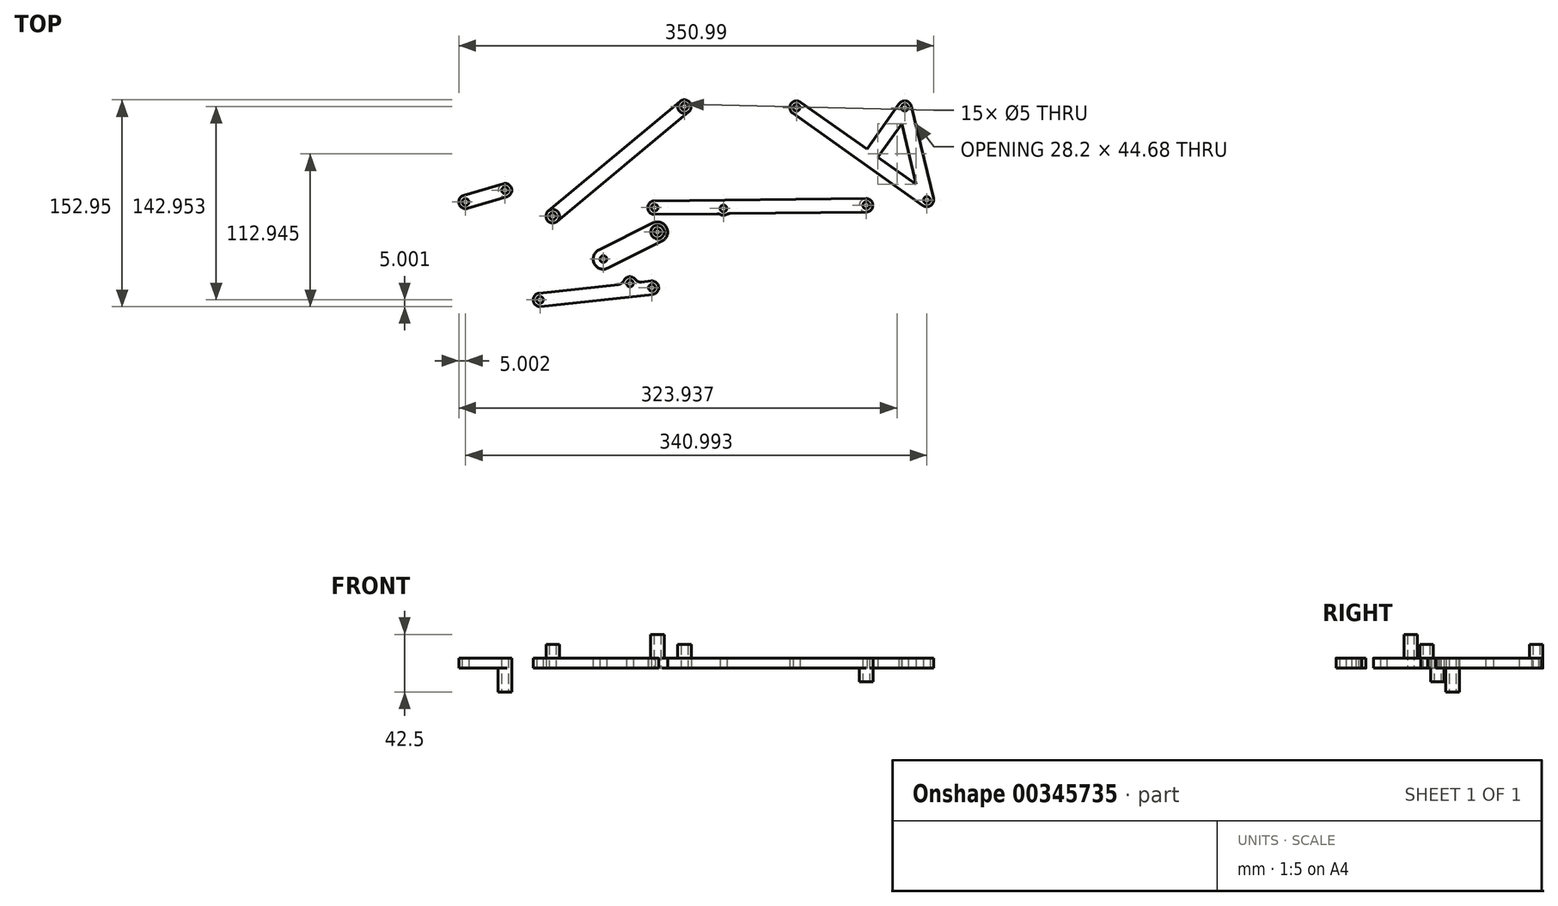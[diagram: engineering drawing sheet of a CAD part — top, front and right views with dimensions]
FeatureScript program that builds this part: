
annotation { "Feature Type Name" : "Feature", "Feature Type Description" : "" }
export const myFeature = defineFeature(function(context is Context, id is Id, definition is map)
    precondition{}
    {
        {
            var Q0;
            Q0=qCreatedBy(makeId("Top.planeOp"),FACE);
            var sketch = newSketch(context, id + "F0", { "sketchPlane" : qUnion([Q0])});
            skLineSegment(sketch, "E0", {"start": v(-4.13, -41.2) * mm, "end": v(-86.83, -50.14) * mm});
            skLineSegment(sketch, "E1", {"start": v(-20.32, -38.04) * mm, "end": v(-86.83, -50.14) * mm});
            skLineSegment(sketch, "E2", {"start": v(-20.32, -38.04) * mm, "end": v(-4.13, -41.2) * mm});
            skCircle(sketch, "E3", {"center": v(-20.32, -38.04) * mm, "radius": 2.5 * mm});
            skCircle(sketch, "E4", {"center": v(-86.83, -50.14) * mm, "radius": 2.5 * mm});
            skCircle(sketch, "E5", {"center": v(-4.13, -41.2) * mm, "radius": 2.5 * mm});
            skLineSegment(sketch, "E6", {"start": v(-20.32, -38.04) * mm, "end": v(-19.44, -42.85) * mm});
            skArc(sketch, "E7.0.startCap", {"start": v(-25.3, -38.46) * mm, "mid": v(-20.98, -33.08) * mm, "end": v(-15.4, -37.14) * mm});
            skArc(sketch, "E7.0.endCap", {"start": v(-14.52, -41.96) * mm, "mid": v(-18.55, -47.77) * mm, "end": v(-24.36, -43.75) * mm});
            skLineSegment(sketch, "E7.0.left", {"start": v(-15.4, -37.14) * mm, "end": v(-14.52, -41.96) * mm});
            skLineSegment(sketch, "E7.0.right", {"start": v(-25.24, -38.93) * mm, "end": v(-24.36, -43.75) * mm});
            skArc(sketch, "E7.1.startCap", {"start": v(-4.66, -36.23) * mm, "mid": v(0.85, -40.66) * mm, "end": v(-3.59, -46.17) * mm});
            skArc(sketch, "E7.1.endCap", {"start": v(-86.3, -55.1) * mm, "mid": v(-91.8, -50.68) * mm, "end": v(-87.37, -45.17) * mm});
            skLineSegment(sketch, "E7.1.left", {"start": v(-3.59, -46.17) * mm, "end": v(-86.3, -55.1) * mm});
            skLineSegment(sketch, "E7.1.right", {"start": v(-4.66, -36.23) * mm, "end": v(-15.35, -37.38) * mm});
            skLineSegment(sketch, "E8.trimOffspring", {"start": v(-25.3, -38.46) * mm, "end": v(-87.37, -45.17) * mm});
            skLineSegment(sketch, "E9.trimOffspring", {"start": v(-17.85, -37.65) * mm, "end": v(-22.81, -38.19) * mm});
            skSolve(sketch);
        }
        {
            var Q0;
            Q0 = qSketchRegion(id + "F0", true);
            var Q1;
            {var subQ0=sQuery(id+"F0.wireOp",EDGE,"E7.0.right");var subQ1=sQuery(id+"F0.wireOp",EDGE,"E0");var subQ2=makeQuery(id+"F0.imprint","INTERSECT",VERTEX,{"derivedFrom":[subQ1,subQ0]});Q1=makeQuery(id+"F0.imprint","IMPRINT",FACE,{"disambiguationData":[TD([[makeQuery(id+"F0.imprint","IMPRINT",EDGE,{"disambiguationData":[TD([[subQ2,-1.0]])],"derivedFrom":subQ1}),-1.0]])]});}
            var Q2;
            {var subQ0=sQuery(id+"F0.wireOp",EDGE,"E6");var subQ1=sQuery(id+"F0.wireOp",EDGE,"E0");var subQ2=makeQuery(id+"F0.imprint","INTERSECT",VERTEX,{"derivedFrom":[subQ1,subQ0]});Q2=makeQuery(id+"F0.imprint","IMPRINT",FACE,{"disambiguationData":[TD([[makeQuery(id+"F0.imprint","IMPRINT",EDGE,{"disambiguationData":[TD([[subQ2,-1.0]])],"derivedFrom":subQ1}),-1.0]])]});}
            var Q3;
            {var subQ0=sQuery(id+"F0.wireOp",EDGE,"E6");var subQ1=sQuery(id+"F0.wireOp",EDGE,"E0");var subQ2=makeQuery(id+"F0.imprint","INTERSECT",VERTEX,{"derivedFrom":[subQ1,subQ0]});Q3=makeQuery(id+"F0.imprint","IMPRINT",FACE,{"disambiguationData":[TD([[makeQuery(id+"F0.imprint","IMPRINT",EDGE,{"disambiguationData":[TD([[subQ2,1.0]])],"derivedFrom":subQ1}),-1.0]])]});}
            var Q4;
            {var subQ3=sQuery(id+"F0.wireOp",EDGE,"E5");var subQ5=sQuery(id+"F0.wireOp",EDGE,"E0");var subQ6=makeQuery(id+"F0.imprint","INTERSECT",VERTEX,{"derivedFrom":[subQ5,subQ3]});Q4=makeQuery(id+"F0.imprint","IMPRINT",FACE,{"disambiguationData":[TD([[makeQuery(id+"F0.imprint","IMPRINT",EDGE,{"disambiguationData":[TD([[subQ6,-1.0]])],"derivedFrom":subQ5}),-1.0]])]});}
            extrude(context, id + "F1", {"entities" : qUnion([Q0, Q1, Q2, Q3, Q4]), "depth" : 7.5 * mm});
        }
        {
            var Q0;
            Q0=makeQuery(id+"F1.opExtrude","SWEPT_EDGE",EDGE,{"disambiguationData":[OSD([sQuery(id+"F0.wireOp",EDGE,"E7.0.left"),sQuery(id+"F0.wireOp",EDGE,"E7.1.right")])]});
            var Q1;
            Q1=makeQuery(id+"F1.opExtrude","SWEPT_EDGE",EDGE,{"disambiguationData":[OSD([sQuery(id+"F0.wireOp",EDGE,"E7.0.startCap"),sQuery(id+"F0.wireOp",EDGE,"E8.trimOffspring")])]});
            fillet(context, id + "F2", {"entities" : qUnion([Q0, Q1]), "radius" : 5 * mm, "tangentPropagation" : true, "allowEdgeOverflow" : false});
        }
        {
            var Q0;
            Q0=qCreatedBy(makeId("Top.planeOp"),FACE);
            var sketch = newSketch(context, id + "F3", { "sketchPlane" : qUnion([Q0])});
            skLineSegment(sketch, "E10", {"start": v(-2.13, 18.04) * mm, "end": v(154.22, 19.78) * mm});
            skLineSegment(sketch, "E11", {"start": v(48.77, 17.41) * mm, "end": v(-2.13, 18.04) * mm});
            skLineSegment(sketch, "E12", {"start": v(48.77, 17.41) * mm, "end": v(154.22, 19.78) * mm});
            skCircle(sketch, "E13", {"center": v(-2.13, 18.04) * mm, "radius": 2.5 * mm});
            skCircle(sketch, "E14", {"center": v(48.77, 17.41) * mm, "radius": 2.5 * mm});
            skCircle(sketch, "E15", {"center": v(154.22, 19.78) * mm, "radius": 2.5 * mm});
            skLineSegment(sketch, "E16", {"start": v(48.77, 17.41) * mm, "end": v(48.75, 18.6) * mm});
            skArc(sketch, "E17.0.startCap", {"start": v(-2.07, 13.04) * mm, "mid": v(-7.13, 17.99) * mm, "end": v(-2.18, 23.04) * mm});
            skArc(sketch, "E17.0.endCap", {"start": v(154.16, 24.78) * mm, "mid": v(159.22, 19.83) * mm, "end": v(154.28, 14.78) * mm});
            skLineSegment(sketch, "E17.0.left", {"start": v(-2.18, 23.04) * mm, "end": v(154.16, 24.78) * mm});
            skLineSegment(sketch, "E17.0.right", {"start": v(-2.07, 13.04) * mm, "end": v(154.28, 14.78) * mm});
            skArc(sketch, "E17.1.startCap", {"start": v(53.77, 17.53) * mm, "mid": v(48.89, 12.42) * mm, "end": v(43.78, 17.3) * mm});
            skArc(sketch, "E17.1.endCap", {"start": v(43.75, 18.5) * mm, "mid": v(48.64, 23.6) * mm, "end": v(53.75, 18.72) * mm});
            skLineSegment(sketch, "E17.1.left", {"start": v(43.78, 17.3) * mm, "end": v(43.75, 18.5) * mm});
            skLineSegment(sketch, "E17.1.right", {"start": v(53.77, 17.53) * mm, "end": v(53.75, 18.72) * mm});
            skSolve(sketch);
        }
        {
            var Q0;
            Q0 = qSketchRegion(id + "F3", true);
            var Q1;
            {var subQ0=sQuery(id+"F3.wireOp",EDGE,"E17.1.right");var subQ1=sQuery(id+"F3.wireOp",EDGE,"E10");var subQ2=makeQuery(id+"F3.imprint","INTERSECT",VERTEX,{"derivedFrom":[subQ1,subQ0]});Q1=makeQuery(id+"F3.imprint","IMPRINT",FACE,{"disambiguationData":[TD([[makeQuery(id+"F3.imprint","IMPRINT",EDGE,{"disambiguationData":[TD([[subQ2,-1.0]])],"derivedFrom":subQ1}),-1.0]])]});}
            var Q2;
            {var subQ1=sQuery(id+"F3.wireOp",EDGE,"E17.1.endCap");var subQ3=sQuery(id+"F3.wireOp",EDGE,"E10");var subQ4=makeQuery(id+"F3.imprint","INTERSECT",VERTEX,{"derivedFrom":[subQ3,subQ1]});Q2=makeQuery(id+"F3.imprint","IMPRINT",FACE,{"disambiguationData":[TD([[makeQuery(id+"F3.imprint","IMPRINT",EDGE,{"disambiguationData":[TD([[subQ4,-1.0]])],"derivedFrom":subQ3}),-1.0]])]});}
            var Q3;
            {var subQ0=sQuery(id+"F3.wireOp",EDGE,"E13");var subQ1=sQuery(id+"F3.wireOp",EDGE,"E10");var subQ2=makeQuery(id+"F3.imprint","INTERSECT",VERTEX,{"derivedFrom":[subQ1,subQ0]});Q3=makeQuery(id+"F3.imprint","IMPRINT",FACE,{"disambiguationData":[TD([[makeQuery(id+"F3.imprint","IMPRINT",EDGE,{"disambiguationData":[TD([[subQ2,-1.0]])],"derivedFrom":subQ1}),-1.0]])]});}
            var Q4;
            {var subQ0=sQuery(id+"F3.wireOp",EDGE,"E14");var subQ1=sQuery(id+"F3.wireOp",EDGE,"E10");var subQ2=makeQuery(id+"F3.imprint","INTERSECT",VERTEX,{"disambiguationData":[OD(1.0)],"derivedFrom":[subQ1,subQ0]});Q4=makeQuery(id+"F3.imprint","IMPRINT",FACE,{"disambiguationData":[TD([[makeQuery(id+"F3.imprint","IMPRINT",EDGE,{"disambiguationData":[TD([[subQ2,-1.0]])],"derivedFrom":subQ1}),-1.0]])]});}
            extrude(context, id + "F4", {"entities" : qUnion([Q0, Q1, Q2, Q3, Q4]), "depth" : 7.5 * mm});
        }
        {
            var Q0;
            {var subQ0=sQuery(id+"F3.wireOp",EDGE,"E17.1.startCap");var subQ1=sQuery(id+"F3.wireOp",EDGE,"E17.0.right");Q0=makeQuery(id+"F4.opExtrude","SWEPT_EDGE",EDGE,{"disambiguationData":[OSD([subQ1,subQ0]),TDD([makeQuery(id+"F3.imprint","INTERSECT",VERTEX,{"disambiguationData":[OD(0.0)],"derivedFrom":[subQ1,subQ0]})])]});}
            var Q1;
            {var subQ0=sQuery(id+"F3.wireOp",EDGE,"E17.1.startCap");var subQ1=sQuery(id+"F3.wireOp",EDGE,"E17.0.right");Q1=makeQuery(id+"F4.opExtrude","SWEPT_EDGE",EDGE,{"disambiguationData":[OSD([subQ1,subQ0]),TDD([makeQuery(id+"F3.imprint","INTERSECT",VERTEX,{"disambiguationData":[OD(1.0)],"derivedFrom":[subQ1,subQ0]})])]});}
            fillet(context, id + "F5", {"entities" : qUnion([Q0, Q1]), "radius" : 5 * mm, "tangentPropagation" : true, "allowEdgeOverflow" : false});
        }
        {
            var Q0;
            Q0=qCreatedBy(makeId("Top.planeOp"),FACE);
            var sketch = newSketch(context, id + "F6", { "sketchPlane" : qUnion([Q0])});
            skLineSegment(sketch, "E18", {"start": v(19.9, 92.81) * mm, "end": v(-77.4, 11.71) * mm});
            skLineSegment(sketch, "E19", {"start": v(-141.85, 22.22) * mm, "end": v(-112.7, 30.91) * mm});
            skCircle(sketch, "E20", {"center": v(-141.85, 22.22) * mm, "radius": 2.5 * mm});
            skCircle(sketch, "E21", {"center": v(-112.7, 30.91) * mm, "radius": 2.5 * mm});
            skCircle(sketch, "E22", {"center": v(-77.4, 11.71) * mm, "radius": 2.5 * mm});
            skCircle(sketch, "E23", {"center": v(19.9, 92.81) * mm, "radius": 2.5 * mm});
            skArc(sketch, "E24.0.startCap", {"start": v(16.7, 96.65) * mm, "mid": v(23.74, 96.02) * mm, "end": v(23.1, 88.97) * mm});
            skArc(sketch, "E24.0.endCap", {"start": v(-74.2, 7.87) * mm, "mid": v(-81.23, 8.51) * mm, "end": v(-80.6, 15.55) * mm});
            skLineSegment(sketch, "E24.0.left", {"start": v(23.1, 88.97) * mm, "end": v(-74.2, 7.87) * mm});
            skLineSegment(sketch, "E24.0.right", {"start": v(16.7, 96.65) * mm, "end": v(-80.6, 15.55) * mm});
            skArc(sketch, "E25.0.startCap", {"start": v(-140.42, 17.43) * mm, "mid": v(-146.64, 20.79) * mm, "end": v(-143.28, 27) * mm});
            skArc(sketch, "E25.0.endCap", {"start": v(-114.12, 35.7) * mm, "mid": v(-107.9, 32.34) * mm, "end": v(-111.26, 26.12) * mm});
            skLineSegment(sketch, "E25.0.left", {"start": v(-143.28, 27) * mm, "end": v(-114.12, 35.7) * mm});
            skLineSegment(sketch, "E25.0.right", {"start": v(-140.42, 17.43) * mm, "end": v(-111.26, 26.12) * mm});
            skSolve(sketch);
        }
        {
            var Q0;
            Q0 = qSketchRegion(id + "F6", true);
            extrude(context, id + "F7", {"entities" : qUnion([Q0]), "depth" : 7.5 * mm});
        }
        {
            var Q0;
            Q0=qCreatedBy(makeId("Top.planeOp"),FACE);
            var sketch = newSketch(context, id + "F8", { "sketchPlane" : qUnion([Q0])});
            skLineSegment(sketch, "E26", {"start": v(199.14, 23.7) * mm, "end": v(102.8, 92) * mm, "construction": true});
            skLineSegment(sketch, "E27", {"start": v(102.8, 92) * mm, "end": v(182.8, 92) * mm, "construction": true});
            skLineSegment(sketch, "E28", {"start": v(182.8, 92) * mm, "end": v(199.14, 23.7) * mm, "construction": true});
            skCircle(sketch, "E29", {"center": v(102.8, 92) * mm, "radius": 2.5 * mm});
            skCircle(sketch, "E30", {"center": v(182.8, 92) * mm, "radius": 2.5 * mm});
            skCircle(sketch, "E31", {"center": v(199.14, 23.7) * mm, "radius": 2.5 * mm});
            skArc(sketch, "E32.0.startCap", {"start": v(102.8, 87) * mm, "mid": v(97.8, 92) * mm, "end": v(102.8, 97) * mm});
            skArc(sketch, "E32.0.endCap", {"start": v(182.8, 97) * mm, "mid": v(187.8, 92) * mm, "end": v(182.8, 87) * mm});
            skLineSegment(sketch, "E32.0.left", {"start": v(102.8, 97) * mm, "end": v(182.8, 97) * mm, "construction": true});
            skLineSegment(sketch, "E32.0.right", {"start": v(102.8, 87) * mm, "end": v(182.8, 87) * mm, "construction": true});
            skArc(sketch, "E32.1.startCap", {"start": v(177.93, 90.84) * mm, "mid": v(181.63, 96.86) * mm, "end": v(187.66, 93.17) * mm});
            skArc(sketch, "E32.1.endCap", {"start": v(204, 24.86) * mm, "mid": v(200.3, 18.83) * mm, "end": v(194.28, 22.53) * mm});
            skLineSegment(sketch, "E32.1.left", {"start": v(187.66, 93.17) * mm, "end": v(204, 24.86) * mm});
            skLineSegment(sketch, "E32.1.right", {"start": v(177.93, 90.84) * mm, "end": v(194.28, 22.53) * mm});
            skArc(sketch, "E32.2.startCap", {"start": v(202.04, 27.77) * mm, "mid": v(203.22, 20.8) * mm, "end": v(196.25, 19.61) * mm});
            skArc(sketch, "E32.2.endCap", {"start": v(99.9, 87.92) * mm, "mid": v(98.72, 94.9) * mm, "end": v(105.69, 96.08) * mm});
            skLineSegment(sketch, "E32.2.left", {"start": v(196.25, 19.61) * mm, "end": v(99.9, 87.92) * mm});
            skLineSegment(sketch, "E32.2.right", {"start": v(202.04, 27.77) * mm, "end": v(105.69, 96.08) * mm});
            skLineSegment(sketch, "E33", {"start": v(178.93, 95.17) * mm, "end": v(154.86, 61.22) * mm});
            skLineSegment(sketch, "E34", {"start": v(186.58, 88.74) * mm, "end": v(162.99, 55.46) * mm});
            skSolve(sketch);
        }
        {
            var Q0;
            Q0 = qSketchRegion(id + "F8", true);
            var Q1;
            {var subQ5=sQuery(id+"F8.wireOp",EDGE,"E27");var subQ7=sQuery(id+"F8.wireOp",EDGE,"E32.2.right");var subQ8=makeQuery(id+"F8.imprint","INTERSECT",VERTEX,{"derivedFrom":[subQ5,subQ7]});Q1=makeQuery(id+"F8.imprint","IMPRINT",FACE,{"disambiguationData":[TD([[makeQuery(id+"F8.imprint","IMPRINT",EDGE,{"disambiguationData":[TD([[subQ8,-1.0]])],"derivedFrom":subQ5}),-1.0]])]});}
            var Q2;
            {var subQ0=sQuery(id+"F8.wireOp",EDGE,"E32.1.right");var subQ1=sQuery(id+"F8.wireOp",EDGE,"E26");var subQ2=makeQuery(id+"F8.imprint","INTERSECT",VERTEX,{"derivedFrom":[subQ1,subQ0]});Q2=makeQuery(id+"F8.imprint","IMPRINT",FACE,{"disambiguationData":[TD([[makeQuery(id+"F8.imprint","IMPRINT",EDGE,{"disambiguationData":[TD([[subQ2,-1.0]])],"derivedFrom":subQ1}),-1.0]])]});}
            var Q3;
            {var subQ5=sQuery(id+"F8.wireOp",EDGE,"E32.0.endCap");var subQ7=sQuery(id+"F8.wireOp",EDGE,"E28");var subQ8=makeQuery(id+"F8.imprint","INTERSECT",VERTEX,{"derivedFrom":[subQ7,subQ5]});Q3=makeQuery(id+"F8.imprint","IMPRINT",FACE,{"disambiguationData":[TD([[makeQuery(id+"F8.imprint","IMPRINT",EDGE,{"disambiguationData":[TD([[subQ8,-1.0]])],"derivedFrom":subQ7}),-1.0]])]});}
            var Q4;
            {var subQ1=sQuery(id+"F8.wireOp",EDGE,"E27");var subQ11=sQuery(id+"F8.wireOp",EDGE,"E32.1.startCap");var subQ13=makeQuery(id+"F8.imprint","INTERSECT",VERTEX,{"derivedFrom":[subQ1,subQ11]});Q4=makeQuery(id+"F8.imprint","IMPRINT",FACE,{"disambiguationData":[TD([[makeQuery(id+"F8.imprint","IMPRINT",EDGE,{"disambiguationData":[TD([[subQ13,-1.0]])],"derivedFrom":subQ1}),-1.0]])]});}
            var Q5;
            {var subQ0=sQuery(id+"F8.wireOp",EDGE,"E31");var subQ1=sQuery(id+"F8.wireOp",EDGE,"E26");var subQ2=makeQuery(id+"F8.imprint","INTERSECT",VERTEX,{"derivedFrom":[subQ1,subQ0]});Q5=makeQuery(id+"F8.imprint","IMPRINT",FACE,{"disambiguationData":[TD([[makeQuery(id+"F8.imprint","IMPRINT",EDGE,{"disambiguationData":[TD([[subQ2,-1.0]])],"derivedFrom":subQ1}),-1.0]])]});}
            var Q6;
            {var subQ0=sQuery(id+"F8.wireOp",EDGE,"E34");var subQ1=sQuery(id+"F8.wireOp",EDGE,"E28");var subQ2=makeQuery(id+"F8.imprint","INTERSECT",VERTEX,{"derivedFrom":[subQ1,subQ0]});Q6=makeQuery(id+"F8.imprint","IMPRINT",FACE,{"disambiguationData":[TD([[makeQuery(id+"F8.imprint","IMPRINT",EDGE,{"disambiguationData":[TD([[subQ2,-1.0]])],"derivedFrom":subQ1}),-1.0]])]});}
            var Q7;
            {var subQ0=sQuery(id+"F8.wireOp",EDGE,"E32.0.endCap");var subQ1=sQuery(id+"F8.wireOp",EDGE,"E28");var subQ2=makeQuery(id+"F8.imprint","INTERSECT",VERTEX,{"derivedFrom":[subQ1,subQ0]});Q7=makeQuery(id+"F8.imprint","IMPRINT",FACE,{"disambiguationData":[TD([[makeQuery(id+"F8.imprint","IMPRINT",EDGE,{"disambiguationData":[TD([[subQ2,-1.0]])],"derivedFrom":subQ1}),1.0]])]});}
            extrude(context, id + "F9", {"entities" : qUnion([Q0, Q1, Q2, Q3, Q4, Q5, Q6, Q7]), "depth" : 7.5 * mm});
        }
        {
            var Q0;
            Q0=qCreatedBy(makeId("Top.planeOp"),FACE);
            var sketch = newSketch(context, id + "F10", { "sketchPlane" : qUnion([Q0])});
            skLineSegment(sketch, "E35", {"start": v(0, 0) * mm, "end": v(-40, -20) * mm});
            skCircle(sketch, "E36", {"center": v(0, 0) * mm, "radius": 2.5 * mm});
            skCircle(sketch, "E37", {"center": v(-40, -20) * mm, "radius": 2.5 * mm});
            skArc(sketch, "E38.0.startCap", {"start": v(-3.35, 6.7) * mm, "mid": v(6.7, 3.35) * mm, "end": v(3.35, -6.7) * mm});
            skArc(sketch, "E38.0.endCap", {"start": v(-36.65, -26.7) * mm, "mid": v(-46.7, -23.35) * mm, "end": v(-43.35, -13.3) * mm});
            skLineSegment(sketch, "E38.0.left", {"start": v(3.35, -6.7) * mm, "end": v(-36.65, -26.7) * mm});
            skLineSegment(sketch, "E38.0.right", {"start": v(-3.35, 6.7) * mm, "end": v(-43.35, -13.3) * mm});
            skSolve(sketch);
        }
        {
            var Q0;
            Q0 = qSketchRegion(id + "F10", true);
            extrude(context, id + "F11", {"entities" : qUnion([Q0]), "depth" : 7.5 * mm});
        }
        {
            var Q0;
            Q0=makeQuery(id+"F7.opExtrude","CAP_FACE",FACE,{"disambiguationData":[OSD([sQuery(id+"F6.wireOp",EDGE,"E22"),sQuery(id+"F6.wireOp",EDGE,"E23"),sQuery(id+"F6.wireOp",EDGE,"E24.0.startCap"),sQuery(id+"F6.wireOp",EDGE,"E24.0.endCap"),sQuery(id+"F6.wireOp",EDGE,"E24.0.left"),sQuery(id+"F6.wireOp",EDGE,"E24.0.right")])],"isStart":false});
            var sketch = newSketch(context, id + "F12", { "sketchPlane" : qUnion([Q0])});
            skArc(sketch, "E39.0", {"start": v(16.7, 96.65) * mm, "mid": v(23.74, 96.02) * mm, "end": v(23.1, 88.97) * mm});
            skCircle(sketch, "E39.1", {"center": v(19.9, 92.81) * mm, "radius": 2.5 * mm});
            skCircle(sketch, "E40", {"center": v(19.9, 92.81) * mm, "radius": 5 * mm});
            skSolve(sketch);
        }
        {
            var Q0;
            Q0 = qSketchRegion(id + "F12", true);
            extrude(context, id + "F13", {"entities" : qUnion([Q0]), "operationType" : NewBodyOperationType.ADD, "depth" : 10 * mm});
        }
        {
            var Q0;
            Q0=makeQuery(id+"F4.opExtrude","CAP_FACE",FACE,{"disambiguationData":[OSD([sQuery(id+"F3.wireOp",EDGE,"E13"),sQuery(id+"F3.wireOp",EDGE,"E14"),sQuery(id+"F3.wireOp",EDGE,"E15"),sQuery(id+"F3.wireOp",EDGE,"E17.0.startCap"),sQuery(id+"F3.wireOp",EDGE,"E17.0.endCap"),sQuery(id+"F3.wireOp",EDGE,"E17.0.left"),sQuery(id+"F3.wireOp",EDGE,"E17.0.right"),sQuery(id+"F3.wireOp",EDGE,"E17.1.startCap")])],"isStart":true});
            var sketch = newSketch(context, id + "F14", { "sketchPlane" : qUnion([Q0])});
            skCircle(sketch, "E41.0", {"center": v(154.22, -19.78) * mm, "radius": 2.5 * mm});
            skArc(sketch, "E41.1", {"start": v(154.16, -24.78) * mm, "mid": v(159.22, -19.83) * mm, "end": v(154.28, -14.78) * mm});
            skCircle(sketch, "E42", {"center": v(154.22, -19.78) * mm, "radius": 5 * mm});
            skSolve(sketch);
        }
        {
            var Q0;
            Q0 = qSketchRegion(id + "F14", true);
            extrude(context, id + "F15", {"entities" : qUnion([Q0]), "operationType" : NewBodyOperationType.ADD, "depth" : 10 * mm});
        }
        {
            var Q0;
            Q0=makeQuery(id+"F7.opExtrude","CAP_FACE",FACE,{"disambiguationData":[OSD([sQuery(id+"F6.wireOp",EDGE,"E20"),sQuery(id+"F6.wireOp",EDGE,"E21"),sQuery(id+"F6.wireOp",EDGE,"E25.0.startCap"),sQuery(id+"F6.wireOp",EDGE,"E25.0.endCap"),sQuery(id+"F6.wireOp",EDGE,"E25.0.left"),sQuery(id+"F6.wireOp",EDGE,"E25.0.right")])],"isStart":true});
            var sketch = newSketch(context, id + "F16", { "sketchPlane" : qUnion([Q0])});
            skCircle(sketch, "E43.0", {"center": v(-112.7, -30.91) * mm, "radius": 2.5 * mm});
            skArc(sketch, "E43.1", {"start": v(-114.12, -35.7) * mm, "mid": v(-107.9, -32.34) * mm, "end": v(-111.26, -26.12) * mm});
            skCircle(sketch, "E44", {"center": v(-112.7, -30.91) * mm, "radius": 5 * mm});
            skSolve(sketch);
        }
        {
            var Q0;
            Q0 = qSketchRegion(id + "F16", true);
            extrude(context, id + "F17", {"entities" : qUnion([Q0]), "operationType" : NewBodyOperationType.ADD, "depth" : 17.5 * mm});
        }
        {
            var Q0;
            Q0=makeQuery(id+"F7.opExtrude","CAP_FACE",FACE,{"disambiguationData":[OSD([sQuery(id+"F6.wireOp",EDGE,"E22"),sQuery(id+"F6.wireOp",EDGE,"E23"),sQuery(id+"F6.wireOp",EDGE,"E24.0.startCap"),sQuery(id+"F6.wireOp",EDGE,"E24.0.endCap"),sQuery(id+"F6.wireOp",EDGE,"E24.0.left"),sQuery(id+"F6.wireOp",EDGE,"E24.0.right")])],"isStart":false});
            var sketch = newSketch(context, id + "F18", { "sketchPlane" : qUnion([Q0])});
            skCircle(sketch, "E45.0", {"center": v(-77.4, 11.71) * mm, "radius": 2.5 * mm});
            skArc(sketch, "E45.1", {"start": v(-74.2, 7.87) * mm, "mid": v(-81.23, 8.51) * mm, "end": v(-80.6, 15.55) * mm});
            skCircle(sketch, "E46", {"center": v(-77.4, 11.71) * mm, "radius": 5 * mm});
            skSolve(sketch);
        }
        {
            var Q0;
            Q0 = qSketchRegion(id + "F18", true);
            extrude(context, id + "F19", {"entities" : qUnion([Q0]), "operationType" : NewBodyOperationType.ADD, "depth" : 10 * mm});
        }
        {
            var Q0;
            Q0=makeQuery(id+"F11.opExtrude","CAP_FACE",FACE,{"disambiguationData":[OSD([sQuery(id+"F10.wireOp",EDGE,"E36"),sQuery(id+"F10.wireOp",EDGE,"E37"),sQuery(id+"F10.wireOp",EDGE,"E38.0.startCap"),sQuery(id+"F10.wireOp",EDGE,"E38.0.endCap"),sQuery(id+"F10.wireOp",EDGE,"E38.0.left"),sQuery(id+"F10.wireOp",EDGE,"E38.0.right")])],"isStart":false});
            var sketch = newSketch(context, id + "F20", { "sketchPlane" : qUnion([Q0])});
            skCircle(sketch, "E47.0", {"center": v(0, 0) * mm, "radius": 2.5 * mm});
            skCircle(sketch, "E48", {"center": v(0, 0) * mm, "radius": 5 * mm});
            skSolve(sketch);
        }
        {
            var Q0;
            Q0 = qSketchRegion(id + "F20", true);
            extrude(context, id + "F21", {"entities" : qUnion([Q0]), "operationType" : NewBodyOperationType.ADD, "depth" : 17.5 * mm});
        }
    });
